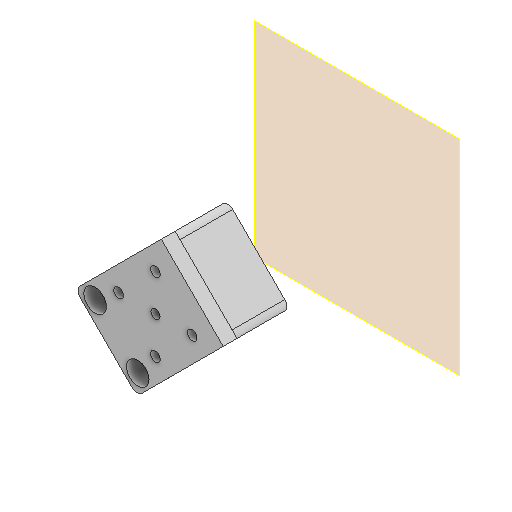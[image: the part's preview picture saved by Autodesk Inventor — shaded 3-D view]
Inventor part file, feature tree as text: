
AUTODESK INVENTOR PART (.ipt)
format: ipt  version: 2022 (Build 260153000, 153)  size: 246,272 bytes
history: native  units: mm
features: extrude x6, sketch x6, reference x3, projected_geometry x3, other x3, plane x1
ambient origin geometry x8: Origin, YZ Plane, XZ Plane, XY Plane, X Axis, Y Axis, Z Axis, Center Point
bodies: Volumenkörper1 (feature_tree)
feature tree (22):
  plane  "Arbeitsebene1"
  extrude  "Extrusion1"  Depth=2.0mm
  extrude  "Extrusion2"  Depth=4.0mm TaperAngle=0.0deg
  extrude  "Extrusion3"  Depth=4.0mm
  extrude  "Extrusion4"  TaperAngle=30.0deg  [1 undecoded]
  extrude  "Extrusion5"  TaperAngle=0.0deg  [1 undecoded]
  extrude  "Extrusion6"  Depth=2.0mm
  sketch  "Skizze1"  dims[d0=7.5mm d1=2.0mm]
  reference  "Referenz1"
  sketch  "Skizze2"  dims[d2=50.0mm d3=0.0mm d4=4.0mm d5=0.0mm]
  reference  "Referenz2"
  projected_geometry  "Projizierte Kontur1"
  sketch  "Skizze3"  dims[d6=4.0mm d7=0.0mm d8=5.0mm]
  reference  "Referenz3"
  projected_geometry  "Projizierte Kontur2"
  sketch  "Skizze4"  dims[d9=3.0mm d10=30.0deg]
  projected_geometry  "Projizierte Kontur3"
  sketch  "Skizze5"  dims[d11=30.0deg d12=0.0mm d13=0.0mm]
  sketch  "Skizze6"  dims[d14=2.8mm d15=2.8mm d16=2.8mm d17=2.8mm d19=6.5mm d20=6.5mm d21=30.0mm d22=0.0mm d23=1.0mm d24=2.0mm d25=20.0mm d26=50.0mm d27=0.0mm]
  other  "Assembly_Matchboxscope_injectionmolded.iam"
  other  "IM_Matchboxscope_plate:2"
  other  "00_Neopixel_4x4_Matrix:1"
note: 2 required parameter values undecoded (feature->parameter linkage not recoverable at this tier; creation-order binding heuristic only, values carry confidence <= 0.55)
